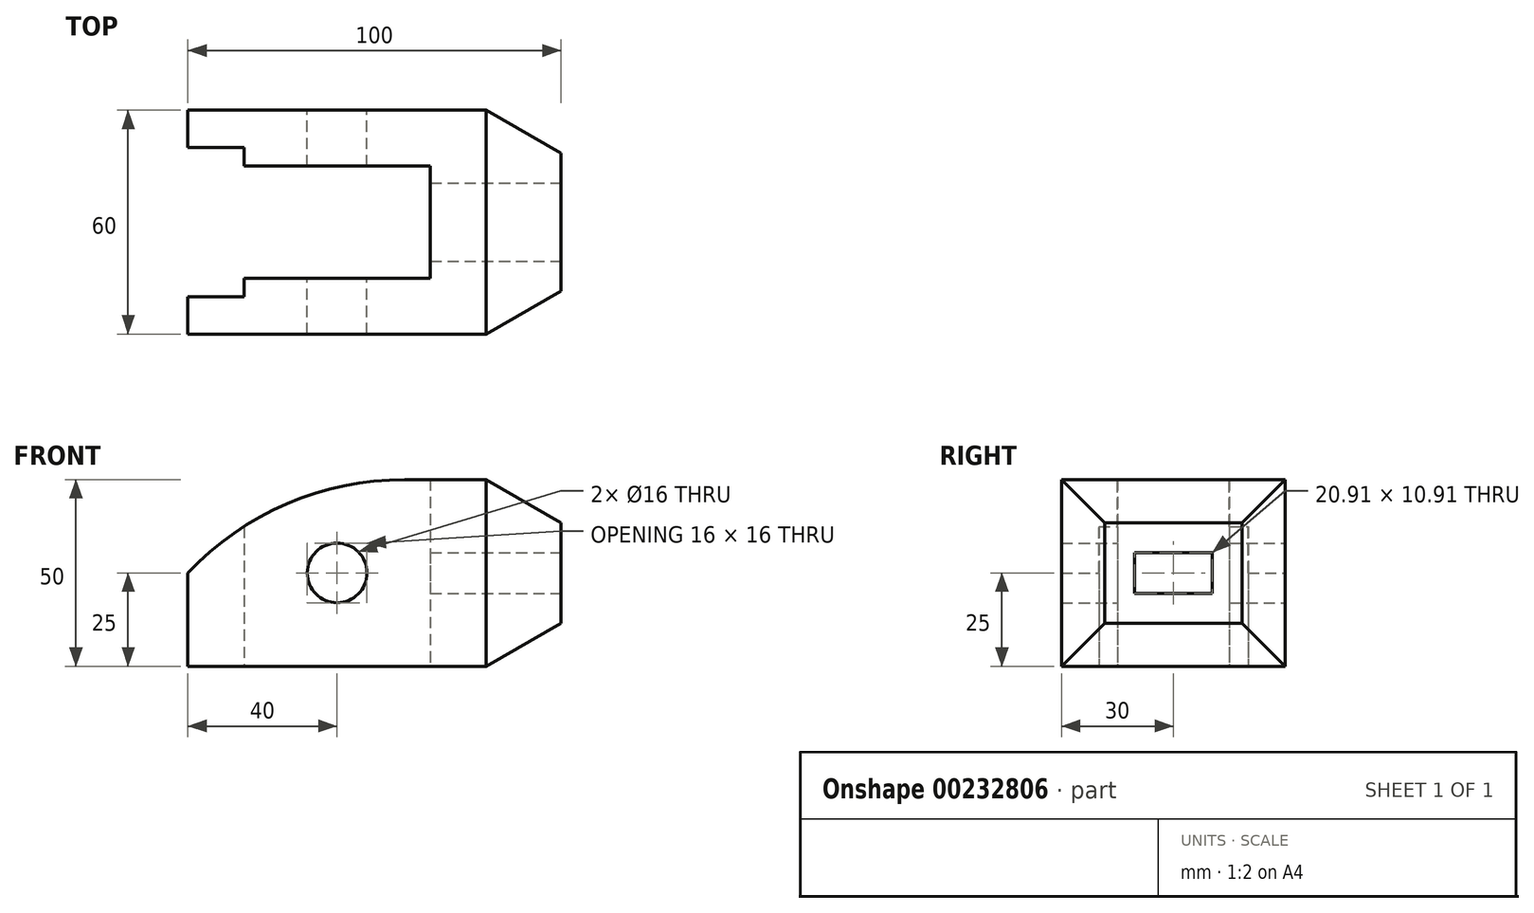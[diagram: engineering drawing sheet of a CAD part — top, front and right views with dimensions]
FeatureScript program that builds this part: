
annotation { "Feature Type Name" : "Feature", "Feature Type Description" : "" }
export const myFeature = defineFeature(function(context is Context, id is Id, definition is map)
    precondition{}
    {
        {
            var Q0;
            Q0=qCreatedBy(makeId("Front.planeOp"),FACE);
            var sketch = newSketch(context, id + "F0", { "sketchPlane" : qUnion([Q0])});
            skLineSegment(sketch, "E0", {"start": v(-40, 0) * mm, "end": v(-40, -25) * mm});
            skCircle(sketch, "E1", {"center": v(0, 0) * mm, "radius": 8 * mm});
            skLineSegment(sketch, "E2", {"start": v(-40, -25) * mm, "end": v(40, -25) * mm});
            skLineSegment(sketch, "E3", {"start": v(40, -25) * mm, "end": v(40, 25) * mm});
            skLineSegment(sketch, "E4", {"start": v(40, 25) * mm, "end": v(18.1, 25) * mm});
            skArc(sketch, "E5", {"start": v(18.1, 25) * mm, "mid": v(-13.53, 18.48) * mm, "end": v(-40, 0) * mm});
            skSolve(sketch);
        }
        {
            var Q0;
            Q0=makeQuery(id+"F0.imprint","IMPRINT",FACE,{"disambiguationData":[TD([[makeQuery(id+"F0.imprint","IMPRINT",EDGE,{"derivedFrom":sQuery(id+"F0.wireOp",EDGE,"E0")}),1.0]])]});
            extrude(context, id + "F1", {"entities" : qUnion([Q0]), "depth" : 60 * mm});
        }
        {
            var Q0;
            Q0=makeQuery(id+"F1.opExtrude","CAP_FACE",FACE,{"disambiguationData":[OSD([sQuery(id+"F0.wireOp",EDGE,"E0"),sQuery(id+"F0.wireOp",EDGE,"E1"),sQuery(id+"F0.wireOp",EDGE,"E2"),sQuery(id+"F0.wireOp",EDGE,"E3"),sQuery(id+"F0.wireOp",EDGE,"E4"),sQuery(id+"F0.wireOp",EDGE,"E5")])],"isStart":false});
            cPlane(context, id + "F2", {"entities" : qUnion([Q0]), "cplaneType" : CPlaneType.OFFSET, "offset" : 0 * mm, "width" : 150 * mm, "height" : 150 * mm});
        }
        {
            var Q0;
            Q0=qCreatedBy(id+"F2.planeOp",FACE);
            var sketch = newSketch(context, id + "F3", { "sketchPlane" : qUnion([Q0])});
            skPoint(sketch, "E6.0", {"position": v(40, -25) * mm});
            skLineSegment(sketch, "E7", {"start": v(40, -25) * mm, "end": v(60, -25) * mm});
            skLineSegment(sketch, "E8", {"start": v(40, -25) * mm, "end": v(60, -13.45) * mm});
            skLineSegment(sketch, "E9.MirrorCS", {"start": v(40, 25) * mm, "end": v(60, 13.45) * mm});
            skLineSegment(sketch, "E10.MirrorCS", {"start": v(40, 25) * mm, "end": v(60, 25) * mm});
            skLineSegment(sketch, "E11", {"start": v(60, -25) * mm, "end": v(60, 25) * mm});
            skSolve(sketch);
        }
        {
            var Q0;
            Q0=makeQuery(id+"F1.opExtrude","SWEPT_FACE",FACE,{"disambiguationData":[OSD([sQuery(id+"F0.wireOp",EDGE,"E3")])]});
            cPlane(context, id + "F4", {"entities" : qUnion([Q0]), "cplaneType" : CPlaneType.OFFSET, "offset" : 20 * mm, "width" : 150 * mm, "height" : 150 * mm});
        }
        {
            var Q0;
            Q0=makeQuery(id+"F1.opExtrude","SWEPT_FACE",FACE,{"disambiguationData":[OSD([sQuery(id+"F0.wireOp",EDGE,"E2")])]});
            var sketch = newSketch(context, id + "F5", { "sketchPlane" : qUnion([Q0])});
            skLineSegment(sketch, "E12", {"start": v(40, 0) * mm, "end": v(60, 0) * mm});
            skLineSegment(sketch, "E13", {"start": v(40, 0) * mm, "end": v(60, 11.55) * mm});
            skPoint(sketch, "E14", {"position": v(40, 30) * mm});
            skLineSegment(sketch, "E15.MirrorCS", {"start": v(40, 60) * mm, "end": v(60, 48.45) * mm});
            skLineSegment(sketch, "E16.MirrorCS", {"start": v(40, 60) * mm, "end": v(60, 60) * mm});
            skLineSegment(sketch, "E17", {"start": v(60, 60) * mm, "end": v(60, 0) * mm});
            skPoint(sketch, "E18.0", {"position": v(60, 60) * mm});
            skSolve(sketch);
        }
        {
            var Q0;
            Q0=qCreatedBy(id+"F4.planeOp",FACE);
            var sketch = newSketch(context, id + "F6", { "sketchPlane" : qUnion([Q0])});
            skPoint(sketch, "E19.0", {"position": v(-60, 13.45) * mm});
            skPoint(sketch, "E20.0", {"position": v(-60, -13.45) * mm});
            skPoint(sketch, "E21.0", {"position": v(-48.45, -25) * mm});
            skPoint(sketch, "E22.0", {"position": v(-11.55, -25) * mm});
            skLineSegment(sketch, "E23.bottom", {"start": v(-48.45, -13.45) * mm, "end": v(-11.55, -13.45) * mm});
            skLineSegment(sketch, "E23.top", {"start": v(-48.45, 13.45) * mm, "end": v(-11.55, 13.45) * mm});
            skLineSegment(sketch, "E23.left", {"start": v(-48.45, -13.45) * mm, "end": v(-48.45, 13.45) * mm});
            skLineSegment(sketch, "E23.right", {"start": v(-11.55, -13.45) * mm, "end": v(-11.55, 13.45) * mm});
            skLineSegment(sketch, "E24.bottom", {"start": v(-60, 25.35) * mm, "end": v(0, 25.35) * mm, "construction": true});
            skLineSegment(sketch, "E24.top", {"start": v(-60, -25) * mm, "end": v(0, -25) * mm, "construction": true});
            skLineSegment(sketch, "E24.left", {"start": v(-60, 25.35) * mm, "end": v(-60, -25) * mm, "construction": true});
            skLineSegment(sketch, "E24.right", {"start": v(0, 25.35) * mm, "end": v(0, -25) * mm, "construction": true});
            skLineSegment(sketch, "E25", {"start": v(-40.45, 5.45) * mm, "end": v(-40.45, -5.45) * mm});
            skLineSegment(sketch, "E26", {"start": v(-40.45, 5.45) * mm, "end": v(-19.55, 5.45) * mm});
            skLineSegment(sketch, "E27", {"start": v(-40.45, -5.45) * mm, "end": v(-19.55, -5.45) * mm});
            skLineSegment(sketch, "E28", {"start": v(-19.55, -5.45) * mm, "end": v(-19.55, 5.45) * mm});
            skSolve(sketch);
        }
        {
            var Q0;
            Q0=makeQuery(id+"F1.opExtrude","SWEPT_FACE",FACE,{"disambiguationData":[OSD([sQuery(id+"F0.wireOp",EDGE,"E0")])]});
            var sketch = newSketch(context, id + "F7", { "sketchPlane" : qUnion([Q0])});
            skLineSegment(sketch, "E29.bottom", {"start": v(0, 25.83) * mm, "end": v(60, 25.83) * mm, "construction": true});
            skLineSegment(sketch, "E29.top", {"start": v(0, -25) * mm, "end": v(60, -25) * mm, "construction": true});
            skLineSegment(sketch, "E29.left", {"start": v(0, 25.83) * mm, "end": v(0, -25) * mm, "construction": true});
            skLineSegment(sketch, "E29.right", {"start": v(60, 25.83) * mm, "end": v(60, -25) * mm, "construction": true});
            skLineSegment(sketch, "E30", {"start": v(10, 25.83) * mm, "end": v(10, -25) * mm});
            skLineSegment(sketch, "E31", {"start": v(50, 25.83) * mm, "end": v(50, -25) * mm});
            skLineSegment(sketch, "E32", {"start": v(15, 25.83) * mm, "end": v(15, -25) * mm});
            skLineSegment(sketch, "E33", {"start": v(45, 25.83) * mm, "end": v(45, -25) * mm});
            skLineSegment(sketch, "E34", {"start": v(10, 25.83) * mm, "end": v(50, 25.83) * mm});
            skLineSegment(sketch, "E35", {"start": v(10, -25) * mm, "end": v(50, -25) * mm});
            skSolve(sketch);
        }
        {
            var Q0;
            {var subQ0=sQuery(id+"F7.wireOp",EDGE,"E35");var subQ1=sQuery(id+"F7.wireOp",EDGE,"E32");var subQ2=makeQuery(id+"F7.imprint","INTERSECT",VERTEX,{"derivedFrom":[subQ1,subQ0]});Q0=makeQuery(id+"F7.imprint","IMPRINT",FACE,{"disambiguationData":[TD([[makeQuery(id+"F7.imprint","IMPRINT",EDGE,{"disambiguationData":[TD([[subQ2,1.0]])],"derivedFrom":subQ0}),-1.0]])]});}
            var Q1;
            {var subQ0=sQuery(id+"F7.wireOp",EDGE,"E34");var subQ1=sQuery(id+"F7.wireOp",EDGE,"E32");var subQ2=makeQuery(id+"F7.imprint","INTERSECT",VERTEX,{"derivedFrom":[subQ1,subQ0]});Q1=makeQuery(id+"F7.imprint","IMPRINT",FACE,{"disambiguationData":[TD([[makeQuery(id+"F7.imprint","IMPRINT",EDGE,{"disambiguationData":[TD([[subQ2,-1.0]])],"derivedFrom":subQ0}),-1.0]])]});}
            extrude(context, id + "F8", {"entities" : qUnion([Q0, Q1]), "operationType" : NewBodyOperationType.REMOVE, "oppositeDirection" : true, "depth" : 65 * mm});
        }
        {
            var Q0;
            {var subQ0=sQuery(id+"F7.wireOp",EDGE,"E34");var subQ1=sQuery(id+"F7.wireOp",EDGE,"E30");var subQ2=makeQuery(id+"F7.imprint","INTERSECT",VERTEX,{"derivedFrom":[subQ1,subQ0]});Q0=makeQuery(id+"F7.imprint","IMPRINT",FACE,{"disambiguationData":[TD([[makeQuery(id+"F7.imprint","IMPRINT",EDGE,{"disambiguationData":[TD([[subQ2,-1.0]])],"derivedFrom":subQ0}),-1.0]])]});}
            var Q1;
            {var subQ0=sQuery(id+"F7.wireOp",EDGE,"E35");var subQ6=sQuery(id+"F7.wireOp",EDGE,"E32");var subQ7=makeQuery(id+"F7.imprint","INTERSECT",VERTEX,{"derivedFrom":[subQ6,subQ0]});Q1=makeQuery(id+"F7.imprint","IMPRINT",FACE,{"disambiguationData":[TD([[makeQuery(id+"F7.imprint","IMPRINT",EDGE,{"disambiguationData":[TD([[subQ7,1.0]])],"derivedFrom":subQ6}),-1.0]])]});}
            var Q2;
            {var subQ0=sQuery(id+"F7.wireOp",EDGE,"E34");var subQ1=sQuery(id+"F7.wireOp",EDGE,"E31");var subQ2=makeQuery(id+"F7.imprint","INTERSECT",VERTEX,{"derivedFrom":[subQ1,subQ0]});Q2=makeQuery(id+"F7.imprint","IMPRINT",FACE,{"disambiguationData":[TD([[makeQuery(id+"F7.imprint","IMPRINT",EDGE,{"disambiguationData":[TD([[subQ2,1.0]])],"derivedFrom":subQ0}),-1.0]])]});}
            var Q3;
            {var subQ0=sQuery(id+"F7.wireOp",EDGE,"E35");var subQ6=sQuery(id+"F7.wireOp",EDGE,"E33");var subQ7=makeQuery(id+"F7.imprint","INTERSECT",VERTEX,{"derivedFrom":[subQ6,subQ0]});Q3=makeQuery(id+"F7.imprint","IMPRINT",FACE,{"disambiguationData":[TD([[makeQuery(id+"F7.imprint","IMPRINT",EDGE,{"disambiguationData":[TD([[subQ7,1.0]])],"derivedFrom":subQ6}),1.0]])]});}
            extrude(context, id + "F9", {"entities" : qUnion([Q0, Q1, Q2, Q3]), "operationType" : NewBodyOperationType.REMOVE, "oppositeDirection" : true, "depth" : 15 * mm});
        }
        {
            var Q0;
            Q0=makeQuery(id+"F6.imprint","IMPRINT",FACE,{"disambiguationData":[TD([[makeQuery(id+"F6.imprint","IMPRINT",EDGE,{"derivedFrom":sQuery(id+"F6.wireOp",EDGE,"E25")}),1.0]])]});
            extrude(context, id + "F10", {"entities" : qUnion([Q0]), "operationType" : NewBodyOperationType.REMOVE, "endBound" : BoundingType.THROUGH_ALL, "oppositeDirection" : true, "depth" : 25 * mm});
        }
        {
            var Q0;
            Q0=makeQuery(id+"F1.opExtrude","SWEPT_FACE",FACE,{"disambiguationData":[OSD([sQuery(id+"F0.wireOp",EDGE,"E3")])]});
            extrude(context, id + "F11", {"entities" : qUnion([Q0]), "operationType" : NewBodyOperationType.ADD, "depth" : 20 * mm});
        }
        {
            var Q0;
            {var subQ0=sQuery(id+"F3.wireOp",EDGE,"E9.MirrorCS");Q0=makeQuery(id+"F3.imprint","IMPRINT",FACE,{"disambiguationData":[TD([[makeQuery(id+"F3.imprint","IMPRINT",EDGE,{"derivedFrom":subQ0}),1.0]])]});}
            var Q1;
            {var subQ0=sQuery(id+"F3.wireOp",EDGE,"E7");Q1=makeQuery(id+"F3.imprint","IMPRINT",FACE,{"disambiguationData":[TD([[makeQuery(id+"F3.imprint","IMPRINT",EDGE,{"derivedFrom":subQ0}),1.0]])]});}
            extrude(context, id + "F12", {"entities" : qUnion([Q0, Q1]), "operationType" : NewBodyOperationType.REMOVE, "endBound" : BoundingType.THROUGH_ALL, "oppositeDirection" : true, "depth" : 25 * mm});
        }
        {
            var Q0;
            {var subQ0=sQuery(id+"F5.wireOp",EDGE,"E12");Q0=makeQuery(id+"F5.imprint","IMPRINT",FACE,{"disambiguationData":[TD([[makeQuery(id+"F5.imprint","IMPRINT",EDGE,{"derivedFrom":subQ0}),1.0]])]});}
            var Q1;
            {var subQ0=sQuery(id+"F5.wireOp",EDGE,"E15.MirrorCS");Q1=makeQuery(id+"F5.imprint","IMPRINT",FACE,{"disambiguationData":[TD([[makeQuery(id+"F5.imprint","IMPRINT",EDGE,{"derivedFrom":subQ0}),1.0]])]});}
            extrude(context, id + "F13", {"entities" : qUnion([Q0, Q1]), "operationType" : NewBodyOperationType.REMOVE, "endBound" : BoundingType.THROUGH_ALL, "oppositeDirection" : true, "depth" : 25 * mm});
        }
    });
